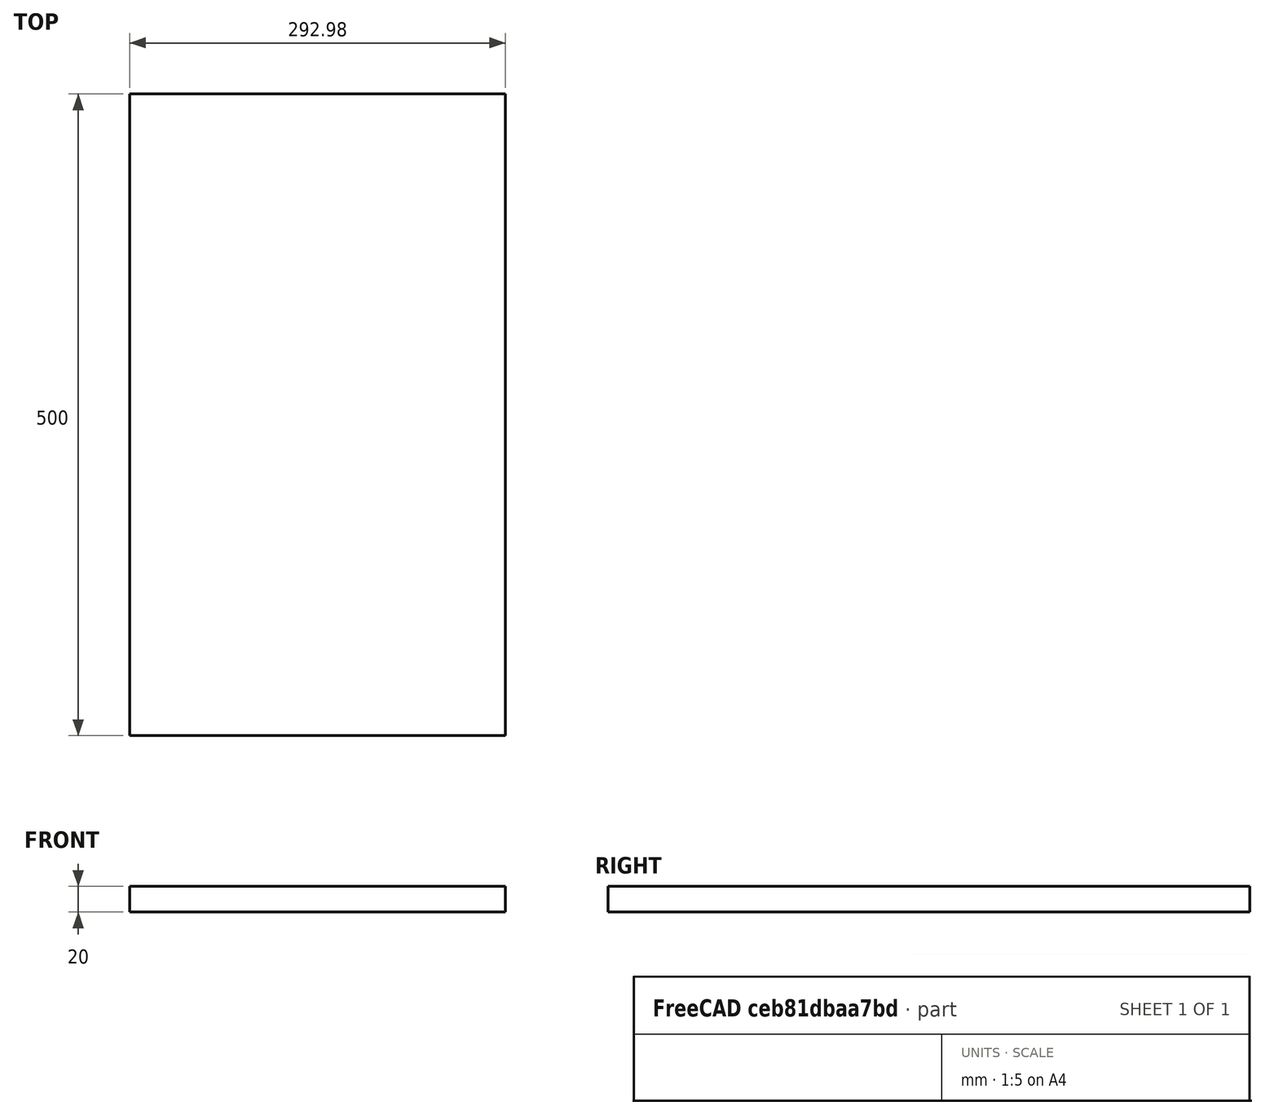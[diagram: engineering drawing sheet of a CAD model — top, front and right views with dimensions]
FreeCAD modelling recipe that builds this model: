
FCSTD DOCUMENT  (FreeCAD 0.19R24212 (Git))
Label: Façade
License: Creative Commons Attribution
LicenseURL: http://creativecommons.org/licenses/by/4.0/
objects: Sketcher::SketchObject×1, PartDesign::Pad×1, PartDesign::CoordinateSystem×1, PartDesign::Body×1
note: 5 computed .brp shape members not serialized (recipe doc carries the construction recipe); baked Part::Feature solids carry a one-line shape summary decoded from their .brp

FEATURE [Sketcher::SketchObject] Sketch
  FullyConstrained = false
  MapMode = 5
  Support = -> [XY_Plane001]
  sketch-geometry (4):
    g0: LineSegment StartX=0 StartY=0 StartZ=0 EndX=292.984 EndY=0 EndZ=0
    g1: LineSegment StartX=292.984 StartY=0 StartZ=0 EndX=292.984 EndY=500 EndZ=0
    g2: LineSegment StartX=292.984 StartY=500 StartZ=0 EndX=0 EndY=500 EndZ=0
    g3: LineSegment StartX=0 StartY=500 StartZ=0 EndX=0 EndY=0 EndZ=0
  constraints (10):
    c: Coincident(g0,g1)
    c: Coincident(g1,g2)
    c: Coincident(g2,g3)
    c: Coincident(g3,g0)
    c: Horizontal(g0)
    c: Horizontal(g2)
    c: Vertical(g1)
    c: Vertical(g3)
    c: Coincident(g0,g-1)
    c: DistanceY(g3,g3) = 500
FEATURE [PartDesign::Pad] Pad
  Direction = (1,1,1)
  Length = 20
  Length2 = 100
  Midplane = true
  Profile = -> Sketch
  Refine = true
  Type = 0
FEATURE [PartDesign::CoordinateSystem] Local_CS
  AttacherType = Attacher::AttachEngine3D
  MapMode = 7
  Placement = pos=(0,500,0) rot=(0,0.707107,0.707107;3.14159rad)
  Support = -> [Sketch]
FEATURE [PartDesign::Body] Body
  Group = -> [Sketch,Pad,Local_CS]
  Origin = -> Origin001
  Tip = -> Pad
